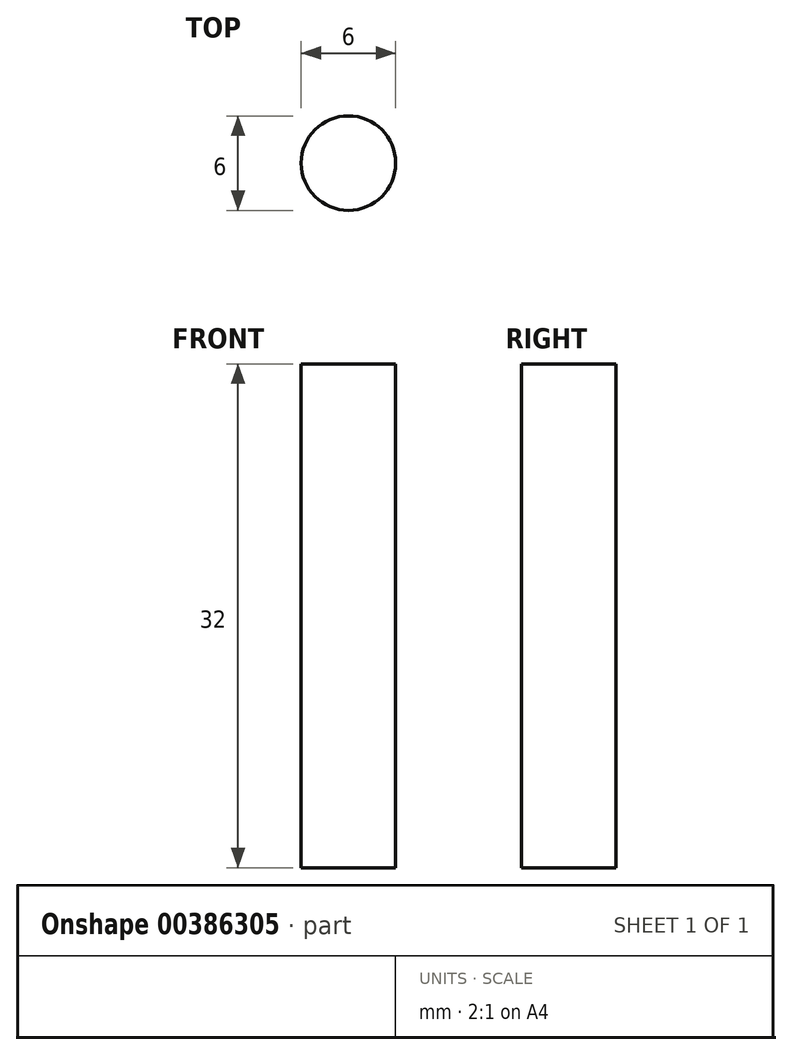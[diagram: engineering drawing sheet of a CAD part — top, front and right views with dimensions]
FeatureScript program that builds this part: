
annotation { "Feature Type Name" : "Feature", "Feature Type Description" : "" }
export const myFeature = defineFeature(function(context is Context, id is Id, definition is map)
    precondition{}
    {
        {
            var Q0;
            Q0=qCreatedBy(makeId("Top.planeOp"),FACE);
            var sketch = newSketch(context, id + "F0", { "sketchPlane" : qUnion([Q0])});
            skCircle(sketch, "E0", {"center": v(0, 0) * mm, "radius": 3 * mm});
            skSolve(sketch);
        }
        {
            var Q0;
            Q0=makeQuery(id+"F0.imprint","IMPRINT",FACE,{"disambiguationData":[TD([[makeQuery(id+"F0.imprint","IMPRINT",EDGE,{"derivedFrom":sQuery(id+"F0.wireOp",EDGE,"E0")}),1.0]])]});
            extrude(context, id + "F1", {"entities" : qUnion([Q0]), "depth" : 32 * mm});
        }
    });
